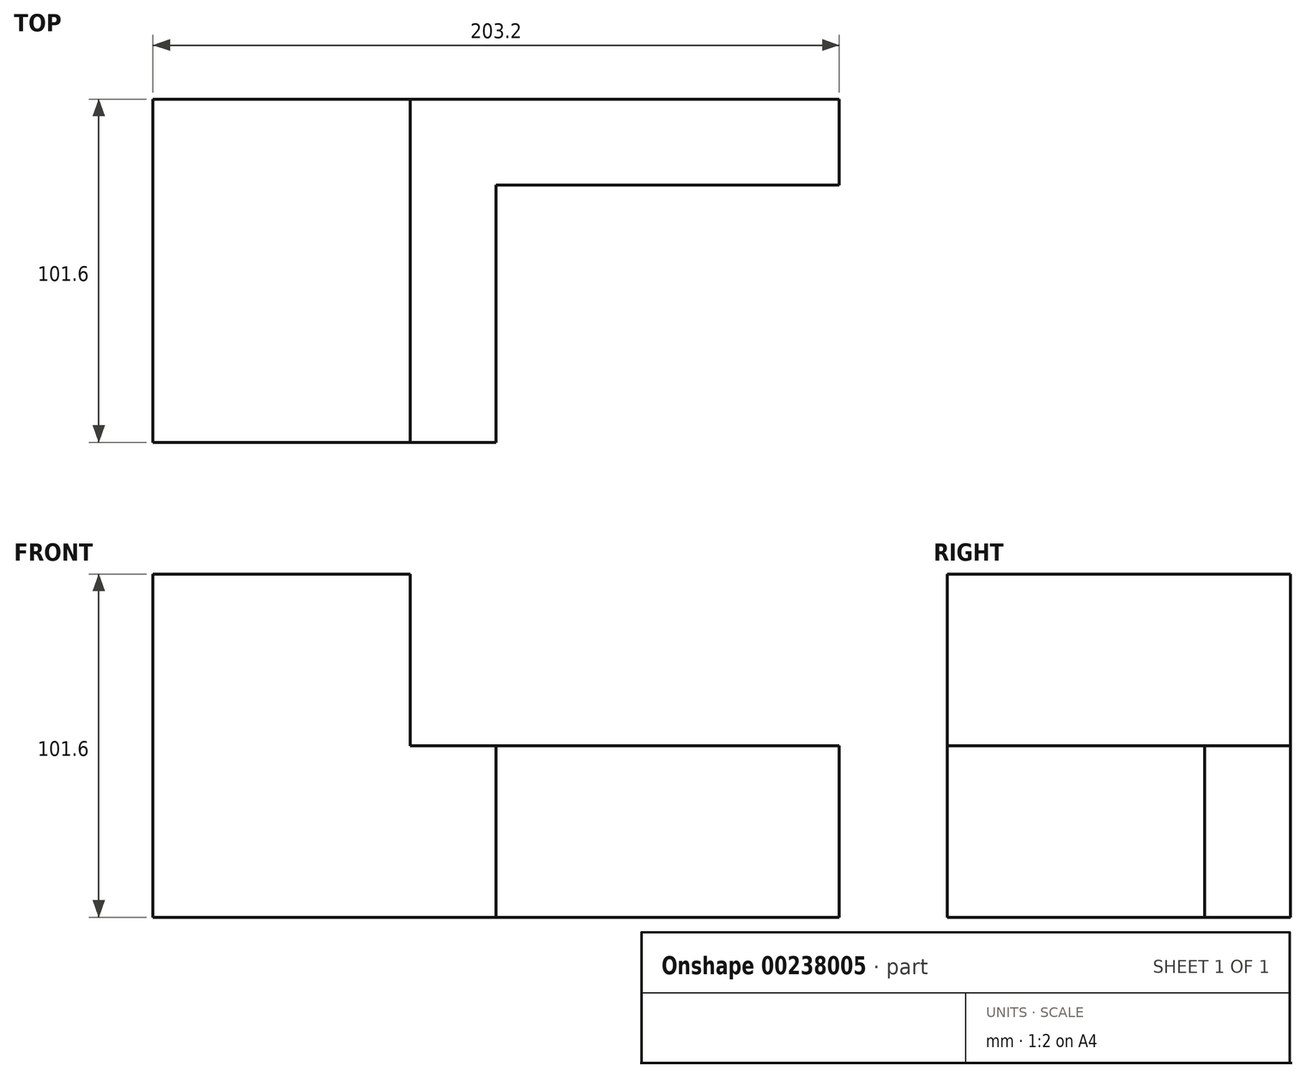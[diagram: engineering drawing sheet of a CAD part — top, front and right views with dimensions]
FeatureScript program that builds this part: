
annotation { "Feature Type Name" : "Feature", "Feature Type Description" : "" }
export const myFeature = defineFeature(function(context is Context, id is Id, definition is map)
    precondition{}
    {
        {
            var Q0;
            Q0=qCreatedBy(makeId("Front.planeOp"),FACE);
            var sketch = newSketch(context, id + "F0", { "sketchPlane" : qUnion([Q0])});
            skLineSegment(sketch, "E0.bottom", {"start": v(-133.04, 66.11) * mm, "end": v(70.16, 66.11) * mm});
            skLineSegment(sketch, "E0.top", {"start": v(-133.04, -35.49) * mm, "end": v(70.16, -35.49) * mm});
            skLineSegment(sketch, "E0.left", {"start": v(-133.04, 66.11) * mm, "end": v(-133.04, -35.49) * mm});
            skLineSegment(sketch, "E0.right", {"start": v(70.16, 66.11) * mm, "end": v(70.16, -35.49) * mm});
            skSolve(sketch);
        }
        {
            var Q0;
            Q0=makeQuery(id+"F0.imprint","IMPRINT",FACE,{"disambiguationData":[TD([[makeQuery(id+"F0.imprint","IMPRINT",EDGE,{"derivedFrom":sQuery(id+"F0.wireOp",EDGE,"E0.bottom")}),-1.0]])]});
            extrude(context, id + "F1", {"entities" : qUnion([Q0]), "depth" : 101.6 * mm});
        }
        {
            var Q0;
            Q0=makeQuery(id+"F1.opExtrude","CAP_FACE",FACE,{"disambiguationData":[OSD([sQuery(id+"F0.wireOp",EDGE,"E0.bottom"),sQuery(id+"F0.wireOp",EDGE,"E0.top"),sQuery(id+"F0.wireOp",EDGE,"E0.left"),sQuery(id+"F0.wireOp",EDGE,"E0.right")])],"isStart":false});
            var sketch = newSketch(context, id + "F2", { "sketchPlane" : qUnion([Q0])});
            skLineSegment(sketch, "E1.bottom", {"start": v(70.16, 66.11) * mm, "end": v(-56.84, 66.11) * mm});
            skLineSegment(sketch, "E1.top", {"start": v(70.16, 15.31) * mm, "end": v(-56.84, 15.31) * mm});
            skLineSegment(sketch, "E1.left", {"start": v(70.16, 66.11) * mm, "end": v(70.16, 15.31) * mm});
            skLineSegment(sketch, "E1.right", {"start": v(-56.84, 66.11) * mm, "end": v(-56.84, 15.31) * mm});
            skSolve(sketch);
        }
        {
            var Q0;
            Q0=makeQuery(id+"F2.imprint","IMPRINT",FACE,{"disambiguationData":[TD([[makeQuery(id+"F2.imprint","IMPRINT",EDGE,{"derivedFrom":sQuery(id+"F2.wireOp",EDGE,"E1.bottom")}),-1.0]])]});
            extrude(context, id + "F3", {"entities" : qUnion([Q0]), "operationType" : NewBodyOperationType.REMOVE, "oppositeDirection" : true, "depth" : 101.6 * mm});
        }
        {
            var Q0;
            Q0=makeQuery(id+"F1.opExtrude","CAP_FACE",FACE,{"disambiguationData":[OSD([sQuery(id+"F0.wireOp",EDGE,"E0.bottom"),sQuery(id+"F0.wireOp",EDGE,"E0.top"),sQuery(id+"F0.wireOp",EDGE,"E0.left"),sQuery(id+"F0.wireOp",EDGE,"E0.right")])],"isStart":false});
            var sketch = newSketch(context, id + "F4", { "sketchPlane" : qUnion([Q0])});
            skLineSegment(sketch, "E2.bottom", {"start": v(70.16, -35.49) * mm, "end": v(-31.44, -35.49) * mm});
            skLineSegment(sketch, "E2.top", {"start": v(70.16, 15.31) * mm, "end": v(-31.44, 15.31) * mm});
            skLineSegment(sketch, "E2.left", {"start": v(70.16, -35.49) * mm, "end": v(70.16, 15.31) * mm});
            skLineSegment(sketch, "E2.right", {"start": v(-31.44, -35.49) * mm, "end": v(-31.44, 15.31) * mm});
            skSolve(sketch);
        }
        {
            var Q0;
            Q0=makeQuery(id+"F4.imprint","IMPRINT",FACE,{"disambiguationData":[TD([[makeQuery(id+"F4.imprint","IMPRINT",EDGE,{"derivedFrom":sQuery(id+"F4.wireOp",EDGE,"E2.bottom")}),1.0]])]});
            extrude(context, id + "F5", {"entities" : qUnion([Q0]), "operationType" : NewBodyOperationType.REMOVE, "oppositeDirection" : true, "depth" : 76.2 * mm});
        }
    });
